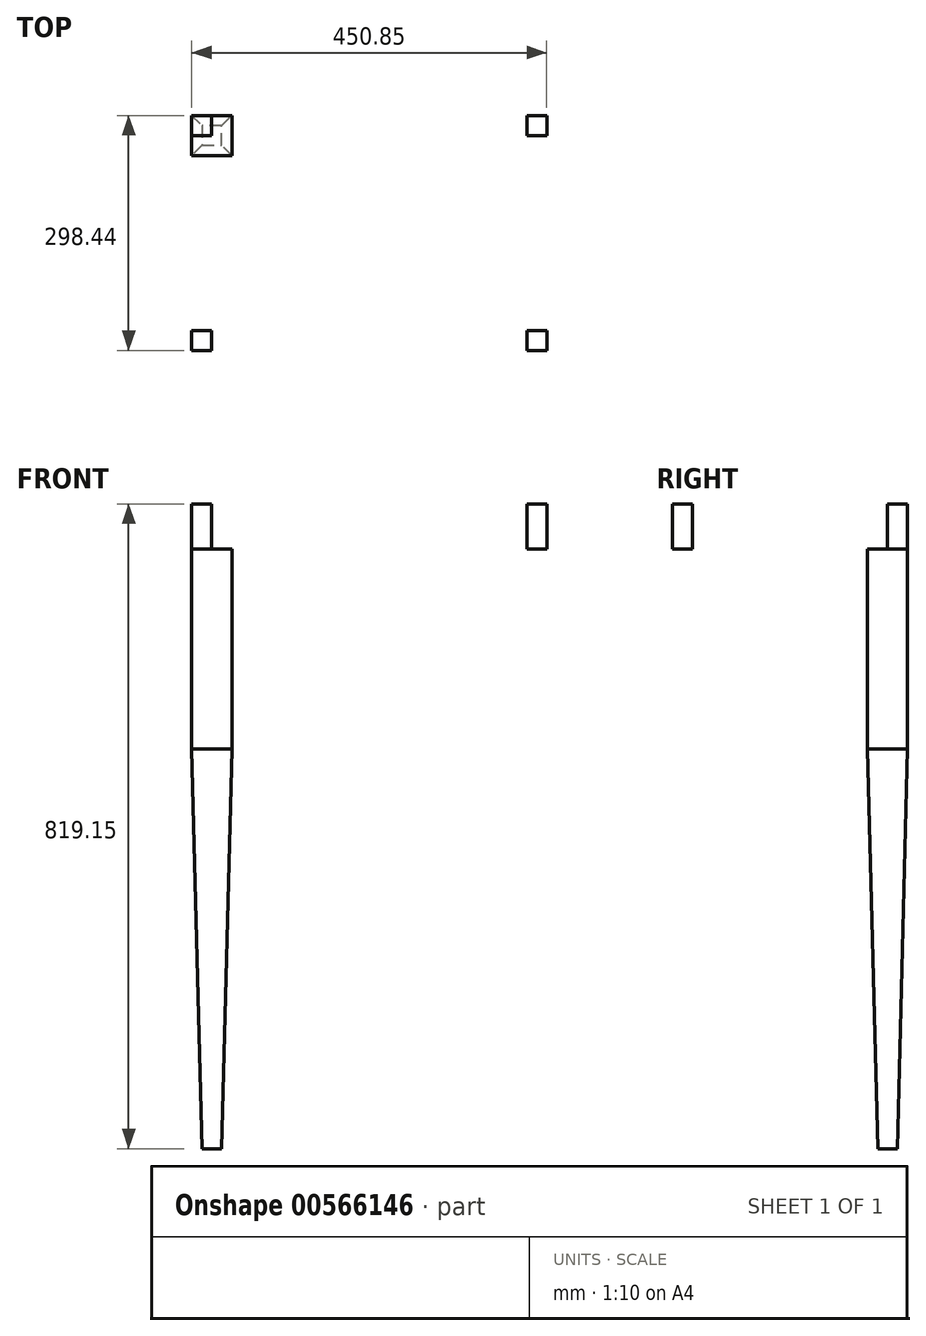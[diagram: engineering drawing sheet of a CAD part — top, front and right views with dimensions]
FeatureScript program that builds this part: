
annotation { "Feature Type Name" : "Feature", "Feature Type Description" : "" }
export const myFeature = defineFeature(function(context is Context, id is Id, definition is map)
    precondition{}
    {
        {
            var Q0;
            Q0=qCreatedBy(makeId("Top.planeOp"),FACE);
            var sketch = newSketch(context, id + "F0", { "sketchPlane" : qUnion([Q0])});
            skLineSegment(sketch, "E0.bottom", {"start": v(-228.6, 152.4) * mm, "end": v(228.6, 152.4) * mm});
            skLineSegment(sketch, "E0.top", {"start": v(-228.6, -152.4) * mm, "end": v(228.6, -152.4) * mm});
            skLineSegment(sketch, "E0.left", {"start": v(-228.6, 152.4) * mm, "end": v(-228.6, -152.4) * mm});
            skLineSegment(sketch, "E0.right", {"start": v(228.6, 152.4) * mm, "end": v(228.6, -152.4) * mm});
            skLineSegment(sketch, "E1", {"start": v(-228.6, -123.82) * mm, "end": v(-200.02, -123.82) * mm});
            skLineSegment(sketch, "E2", {"start": v(-200.02, -123.83) * mm, "end": v(-200.02, -152.4) * mm});
            skLineSegment(sketch, "E3", {"start": v(-228.6, 123.83) * mm, "end": v(-200.03, 123.83) * mm});
            skLineSegment(sketch, "E4", {"start": v(-200.03, 123.83) * mm, "end": v(-200.03, 152.4) * mm});
            skLineSegment(sketch, "E5", {"start": v(200.03, 152.4) * mm, "end": v(200.03, 123.83) * mm});
            skLineSegment(sketch, "E6", {"start": v(200.03, 123.82) * mm, "end": v(228.6, 123.82) * mm});
            skLineSegment(sketch, "E7", {"start": v(228.6, -123.82) * mm, "end": v(200.03, -123.82) * mm});
            skLineSegment(sketch, "E8", {"start": v(200.03, -123.83) * mm, "end": v(200.03, -152.4) * mm});
            skSolve(sketch);
        }
        {
            var Q0;
            Q0=qCreatedBy(makeId("Top.planeOp"),FACE);
            var sketch = newSketch(context, id + "F1", { "sketchPlane" : qUnion([Q0])});
            skLineSegment(sketch, "E9.bottom", {"start": v(-225.42, 149.22) * mm, "end": v(-174.62, 149.22) * mm});
            skLineSegment(sketch, "E9.top", {"start": v(-225.42, 98.42) * mm, "end": v(-174.62, 98.42) * mm});
            skLineSegment(sketch, "E9.left", {"start": v(-225.42, 149.22) * mm, "end": v(-225.42, 98.42) * mm});
            skLineSegment(sketch, "E9.right", {"start": v(-174.62, 149.22) * mm, "end": v(-174.62, 98.42) * mm});
            skLineSegment(sketch, "E10", {"start": v(-200.02, 149.22) * mm, "end": v(-200.02, 123.82) * mm});
            skLineSegment(sketch, "E11", {"start": v(-200.02, 123.82) * mm, "end": v(-225.42, 123.82) * mm});
            skSolve(sketch);
        }
        {
            var Q0;
            {var subQ2=sQuery(id+"F1.wireOp",EDGE,"E9.top");Q0=makeQuery(id+"F1.imprint","IMPRINT",FACE,{"disambiguationData":[TD([[makeQuery(id+"F1.imprint","IMPRINT",EDGE,{"derivedFrom":subQ2}),1.0]])]});}
            var Q1;
            {var subQ3=sQuery(id+"F1.wireOp",EDGE,"E10");Q1=makeQuery(id+"F1.imprint","IMPRINT",FACE,{"disambiguationData":[TD([[makeQuery(id+"F1.imprint","IMPRINT",EDGE,{"derivedFrom":subQ3}),-1.0]])]});}
            extrude(context, id + "F2", {"entities" : qUnion([Q0, Q1]), "oppositeDirection" : true, "depth" : 254 * mm, "offsetDistance" : 25.4 * mm, "hasSecondDirectionDraft" : true, "secondDirectionDraftAngle" : 3 * degree});
        }
        {
            var Q0;
            {var subQ3=sQuery(id+"F1.wireOp",EDGE,"E10");Q0=makeQuery(id+"F1.imprint","IMPRINT",FACE,{"disambiguationData":[TD([[makeQuery(id+"F1.imprint","IMPRINT",EDGE,{"derivedFrom":subQ3}),-1.0]])]});}
            extrude(context, id + "F3", {"entities" : qUnion([Q0]), "depth" : 57.15 * mm, "offsetDistance" : 25.4 * mm});
        }
        {
            var Q0;
            Q0=makeQuery(id+"F3.opExtrude","SWEPT_BODY",BODY,{"disambiguationData":[OSD([sQuery(id+"F1.wireOp",EDGE,"E9.bottom"),sQuery(id+"F1.wireOp",EDGE,"E9.left"),sQuery(id+"F1.wireOp",EDGE,"E10"),sQuery(id+"F1.wireOp",EDGE,"E11")])]});
            var Q1;
            Q1=qCreatedBy(makeId("Right.planeOp"),FACE);
            mirror(context, id + "F4", {"entities" : qUnion([Q0]), "mirrorPlane" : qUnion([Q1])});
        }
        {
            var Q0;
            Q0=makeQuery(id+"F3.opExtrude","SWEPT_BODY",BODY,{"disambiguationData":[OSD([sQuery(id+"F1.wireOp",EDGE,"E9.bottom"),sQuery(id+"F1.wireOp",EDGE,"E9.left"),sQuery(id+"F1.wireOp",EDGE,"E10"),sQuery(id+"F1.wireOp",EDGE,"E11")])]});
            var Q1;
            Q1=makeQuery(id+"F4.opPattern","COPY",BODY,{"derivedFrom":makeQuery(id+"F3.opExtrude","SWEPT_BODY",BODY,{"disambiguationData":[OSD([sQuery(id+"F1.wireOp",EDGE,"E9.bottom"),sQuery(id+"F1.wireOp",EDGE,"E9.left"),sQuery(id+"F1.wireOp",EDGE,"E10"),sQuery(id+"F1.wireOp",EDGE,"E11")])]}),"instanceName":"1"});
            var Q2;
            Q2=qCreatedBy(makeId("Front.planeOp"),FACE);
            mirror(context, id + "F5", {"entities" : qUnion([Q0, Q1]), "mirrorPlane" : qUnion([Q2])});
        }
        {
            var Q0;
            Q0=makeQuery(id+"F2.opExtrude","CAP_FACE",FACE,{"disambiguationData":[OSD([sQuery(id+"F1.wireOp",EDGE,"E9.bottom"),sQuery(id+"F1.wireOp",EDGE,"E9.top"),sQuery(id+"F1.wireOp",EDGE,"E9.left"),sQuery(id+"F1.wireOp",EDGE,"E9.right")])],"isStart":false});
            var Q1;
            Q1=makeQuery(id+"F4.opPattern","COPY",FACE,{"derivedFrom":makeQuery(id+"F2.opExtrude","CAP_FACE",FACE,{"disambiguationData":[OSD([sQuery(id+"F1.wireOp",EDGE,"E9.bottom"),sQuery(id+"F1.wireOp",EDGE,"E9.top"),sQuery(id+"F1.wireOp",EDGE,"E9.left"),sQuery(id+"F1.wireOp",EDGE,"E9.right")])],"isStart":false}),"instanceName":"1"});
            var Q2;
            Q2=makeQuery(id+"F5.opPattern","COPY",FACE,{"derivedFrom":makeQuery(id+"F4.opPattern","COPY",FACE,{"derivedFrom":makeQuery(id+"F2.opExtrude","CAP_FACE",FACE,{"disambiguationData":[OSD([sQuery(id+"F1.wireOp",EDGE,"E9.bottom"),sQuery(id+"F1.wireOp",EDGE,"E9.top"),sQuery(id+"F1.wireOp",EDGE,"E9.left"),sQuery(id+"F1.wireOp",EDGE,"E9.right")])],"isStart":false}),"instanceName":"1"}),"instanceName":"1"});
            var Q3;
            Q3=makeQuery(id+"F5.opPattern","COPY",FACE,{"derivedFrom":makeQuery(id+"F2.opExtrude","CAP_FACE",FACE,{"disambiguationData":[OSD([sQuery(id+"F1.wireOp",EDGE,"E9.bottom"),sQuery(id+"F1.wireOp",EDGE,"E9.top"),sQuery(id+"F1.wireOp",EDGE,"E9.left"),sQuery(id+"F1.wireOp",EDGE,"E9.right")])],"isStart":false}),"instanceName":"1"});
            extrude(context, id + "F6", {"entities" : qUnion([Q0, Q1, Q2, Q3]), "operationType" : NewBodyOperationType.ADD, "depth" : 508 * mm, "offsetDistance" : 25.4 * mm, "hasDraft" : true, "draftAngle" : 1.5 * degree, "draftPullDirection" : true});
        }
    });
